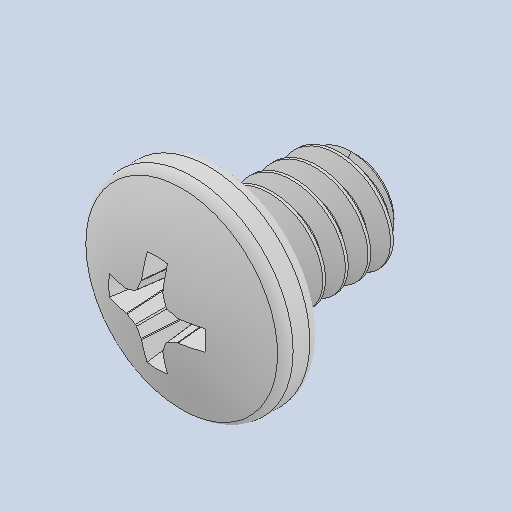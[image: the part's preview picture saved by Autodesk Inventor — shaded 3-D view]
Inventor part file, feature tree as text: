
AUTODESK INVENTOR PART (.ipt)
format: ipt  version: 2022 (Build 260153000, 153)  size: 407,552 bytes
history: native  units: in
note: dims shown in document units (in); Inventor stores cm internally (conversion verified against a paired STEP export)
features: fillet x1
ambient origin geometry x8: Origin, YZ Plane, XZ Plane, XY Plane, X Axis, Y Axis, Z Axis, Center Point
bodies: Solid1 (feature_tree)
feature tree (1):
  fillet  "Fillet1"  [1 undecoded]
note: 1 required parameter value undecoded (feature->parameter linkage not recoverable at this tier; creation-order binding heuristic only, values carry confidence <= 0.55)
